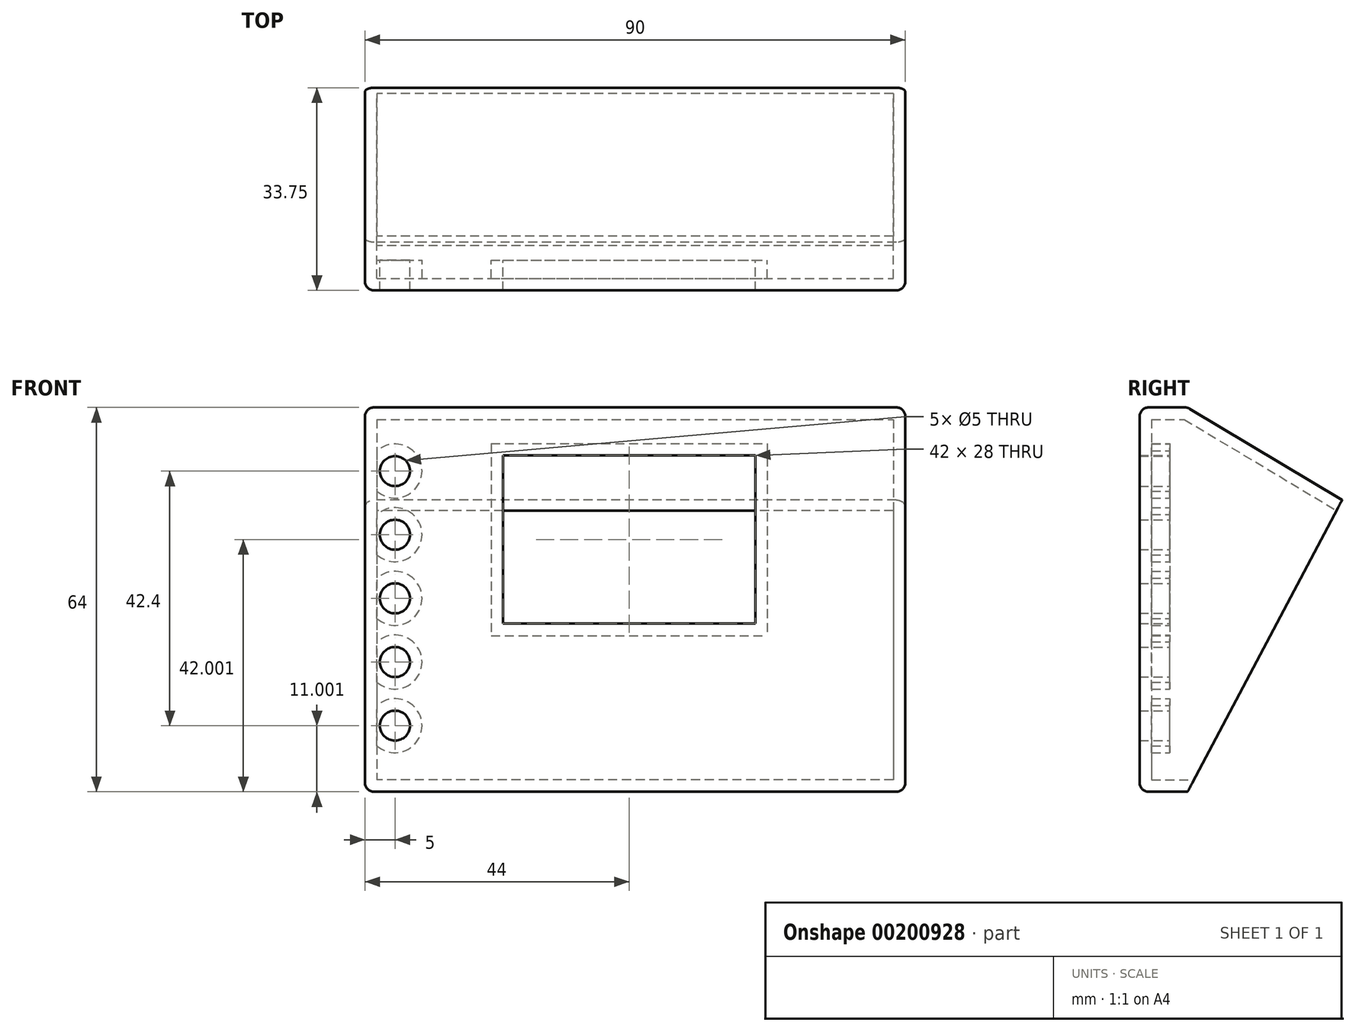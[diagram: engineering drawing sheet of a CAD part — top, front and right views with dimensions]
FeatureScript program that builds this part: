
annotation { "Feature Type Name" : "Feature", "Feature Type Description" : "" }
export const myFeature = defineFeature(function(context is Context, id is Id, definition is map)
    precondition{}
    {
        {
            var Q0;
            Q0=qCreatedBy(makeId("Front.planeOp"),FACE);
            var sketch = newSketch(context, id + "F0", { "sketchPlane" : qUnion([Q0])});
            skLineSegment(sketch, "E0.bottom", {"start": v(-41, 33.96) * mm, "end": v(49, 33.96) * mm});
            skLineSegment(sketch, "E0.top", {"start": v(-41, -30.04) * mm, "end": v(49, -30.04) * mm});
            skLineSegment(sketch, "E0.left", {"start": v(-41, 33.96) * mm, "end": v(-41, -30.04) * mm});
            skLineSegment(sketch, "E0.right", {"start": v(49, 33.96) * mm, "end": v(49, -30.04) * mm});
            skCircle(sketch, "E1", {"center": v(-36, 23.36) * mm, "radius": 2.5 * mm});
            skCircle(sketch, "E2", {"center": v(-36, 12.76) * mm, "radius": 2.5 * mm});
            skCircle(sketch, "E3", {"center": v(-36, 2.16) * mm, "radius": 2.5 * mm});
            skCircle(sketch, "E4", {"center": v(-36, -8.44) * mm, "radius": 2.5 * mm});
            skCircle(sketch, "E5", {"center": v(-36, -19.04) * mm, "radius": 2.5 * mm});
            skLineSegment(sketch, "E6.bottom", {"start": v(-18, 25.96) * mm, "end": v(24, 25.96) * mm});
            skLineSegment(sketch, "E6.top", {"start": v(-18, -2.04) * mm, "end": v(24, -2.04) * mm});
            skLineSegment(sketch, "E6.left", {"start": v(-18, 25.96) * mm, "end": v(-18, -2.04) * mm});
            skLineSegment(sketch, "E6.right", {"start": v(24, 25.96) * mm, "end": v(24, -2.04) * mm});
            skSolve(sketch);
        }
        {
            var Q0;
            Q0=makeQuery(id+"F0.imprint","IMPRINT",FACE,{"disambiguationData":[TD([[makeQuery(id+"F0.imprint","IMPRINT",EDGE,{"derivedFrom":sQuery(id+"F0.wireOp",EDGE,"E0.bottom")}),-1.0]])]});
            extrude(context, id + "F1", {"entities" : qUnion([Q0]), "depth" : 3 * mm});
        }
        {
            var Q0;
            Q0=makeQuery(id+"F1.opExtrude","SWEPT_FACE",FACE,{"disambiguationData":[OSD([sQuery(id+"F0.wireOp",EDGE,"E0.left")])]});
            cPlane(context, id + "F2", {"entities" : qUnion([Q0]), "cplaneType" : CPlaneType.OFFSET, "offset" : 0 * mm, "width" : 150 * mm, "height" : 150 * mm});
        }
        {
            var Q0;
            Q0=qCreatedBy(id+"F2.planeOp",FACE);
            var sketch = newSketch(context, id + "F3", { "sketchPlane" : qUnion([Q0])});
            skLineSegment(sketch, "E7", {"start": v(0, 33.96) * mm, "end": v(-5, 33.96) * mm});
            skLineSegment(sketch, "E8", {"start": v(-5, 33.96) * mm, "end": v(-30.75, 18.56) * mm});
            skLineSegment(sketch, "E9", {"start": v(-30.75, 18.56) * mm, "end": v(-5, -30.04) * mm});
            skLineSegment(sketch, "E10", {"start": v(-5, -30.04) * mm, "end": v(0, -30.04) * mm});
            skLineSegment(sketch, "E11", {"start": v(0, -30.04) * mm, "end": v(0, 33.96) * mm});
            skSolve(sketch);
        }
        {
            var Q0;
            Q0=makeQuery(id+"F3.imprint","IMPRINT",FACE,{"disambiguationData":[TD([[makeQuery(id+"F3.imprint","IMPRINT",EDGE,{"derivedFrom":sQuery(id+"F3.wireOp",EDGE,"E7")}),1.0]])]});
            extrude(context, id + "F4", {"entities" : qUnion([Q0]), "operationType" : NewBodyOperationType.ADD, "oppositeDirection" : true, "depth" : 90 * mm});
        }
        {
            var Q0;
            Q0=makeQuery(id+"F4.opExtrude","SWEPT_FACE",FACE,{"disambiguationData":[OSD([sQuery(id+"F3.wireOp",EDGE,"E9")])]});
            shell(context, id + "F5", {"entities" : qUnion([Q0]), "thickness" : 2 * mm});
        }
        {
            var Q0;
            Q0=makeQuery(id+"F0.imprint","IMPRINT",FACE,{"disambiguationData":[TD([[makeQuery(id+"F0.imprint","IMPRINT",EDGE,{"derivedFrom":sQuery(id+"F0.wireOp",EDGE,"E1")}),1.0]])]});
            var Q1;
            Q1=makeQuery(id+"F0.imprint","IMPRINT",FACE,{"disambiguationData":[TD([[makeQuery(id+"F0.imprint","IMPRINT",EDGE,{"derivedFrom":sQuery(id+"F0.wireOp",EDGE,"E2")}),1.0]])]});
            var Q2;
            Q2=makeQuery(id+"F0.imprint","IMPRINT",FACE,{"disambiguationData":[TD([[makeQuery(id+"F0.imprint","IMPRINT",EDGE,{"derivedFrom":sQuery(id+"F0.wireOp",EDGE,"E3")}),1.0]])]});
            var Q3;
            Q3=makeQuery(id+"F0.imprint","IMPRINT",FACE,{"disambiguationData":[TD([[makeQuery(id+"F0.imprint","IMPRINT",EDGE,{"derivedFrom":sQuery(id+"F0.wireOp",EDGE,"E4")}),1.0]])]});
            var Q4;
            Q4=makeQuery(id+"F0.imprint","IMPRINT",FACE,{"disambiguationData":[TD([[makeQuery(id+"F0.imprint","IMPRINT",EDGE,{"derivedFrom":sQuery(id+"F0.wireOp",EDGE,"E5")}),1.0]])]});
            var Q5;
            Q5=makeQuery(id+"F0.imprint","IMPRINT",FACE,{"disambiguationData":[TD([[makeQuery(id+"F0.imprint","IMPRINT",EDGE,{"derivedFrom":sQuery(id+"F0.wireOp",EDGE,"E6.bottom")}),-1.0]])]});
            extrude(context, id + "F6", {"entities" : qUnion([Q0, Q1, Q2, Q3, Q4, Q5]), "operationType" : NewBodyOperationType.REMOVE, "oppositeDirection" : true, "depth" : 5 * mm});
        }
        {
            var Q0;
            Q0=makeQuery(id+"F1.opExtrude","CAP_EDGE",EDGE,{"disambiguationData":[OSD([sQuery(id+"F0.wireOp",EDGE,"E0.right")])],"isStart":false});
            var Q1;
            Q1=makeQuery(id+"F4.boolean.opBoolean","MERGE",EDGE,{"derivedFrom":[makeQuery(id+"F1.opExtrude","SWEPT_EDGE",EDGE,{"disambiguationData":[OSD([sQuery(id+"F0.wireOp",EDGE,"E0.top"),sQuery(id+"F0.wireOp",EDGE,"E0.right")])]}),makeQuery(id+"F4.opExtrude","CAP_EDGE",EDGE,{"disambiguationData":[OSD([sQuery(id+"F3.wireOp",EDGE,"E10")])],"isStart":false})]});
            var Q2;
            Q2=makeQuery(id+"F1.opExtrude","CAP_EDGE",EDGE,{"disambiguationData":[OSD([sQuery(id+"F0.wireOp",EDGE,"E0.top")])],"isStart":false});
            var Q3;
            Q3=makeQuery(id+"F4.boolean.opBoolean","MERGE",EDGE,{"derivedFrom":[makeQuery(id+"F1.opExtrude","SWEPT_EDGE",EDGE,{"disambiguationData":[OSD([sQuery(id+"F0.wireOp",EDGE,"E0.bottom"),sQuery(id+"F0.wireOp",EDGE,"E0.right")])]}),makeQuery(id+"F4.opExtrude","CAP_EDGE",EDGE,{"disambiguationData":[OSD([sQuery(id+"F3.wireOp",EDGE,"E7")])],"isStart":false})]});
            var Q4;
            Q4=makeQuery(id+"F4.opExtrude","CAP_EDGE",EDGE,{"disambiguationData":[OSD([sQuery(id+"F3.wireOp",EDGE,"E8")])],"isStart":false});
            var Q5;
            Q5=makeQuery(id+"F1.opExtrude","CAP_EDGE",EDGE,{"disambiguationData":[OSD([sQuery(id+"F0.wireOp",EDGE,"E0.bottom")])],"isStart":false});
            var Q6;
            Q6=makeQuery(id+"F4.opExtrude","SWEPT_EDGE",EDGE,{"disambiguationData":[OSD([sQuery(id+"F3.wireOp",EDGE,"E7"),sQuery(id+"F3.wireOp",EDGE,"E8")])]});
            var Q7;
            Q7=makeQuery(id+"F1.opExtrude","CAP_EDGE",EDGE,{"disambiguationData":[OSD([sQuery(id+"F0.wireOp",EDGE,"E0.left")])],"isStart":false});
            var Q8;
            Q8=makeQuery(id+"F4.boolean.opBoolean","MERGE",EDGE,{"derivedFrom":[makeQuery(id+"F1.opExtrude","SWEPT_EDGE",EDGE,{"disambiguationData":[OSD([sQuery(id+"F0.wireOp",EDGE,"E0.bottom"),sQuery(id+"F0.wireOp",EDGE,"E0.left")])]}),makeQuery(id+"F4.opExtrude","CAP_EDGE",EDGE,{"disambiguationData":[OSD([sQuery(id+"F3.wireOp",EDGE,"E7")])],"isStart":true})]});
            var Q9;
            Q9=makeQuery(id+"F4.opExtrude","CAP_EDGE",EDGE,{"disambiguationData":[OSD([sQuery(id+"F3.wireOp",EDGE,"E8")])],"isStart":true});
            var Q10;
            Q10=makeQuery(id+"F4.boolean.opBoolean","MERGE",EDGE,{"derivedFrom":[makeQuery(id+"F1.opExtrude","SWEPT_EDGE",EDGE,{"disambiguationData":[OSD([sQuery(id+"F0.wireOp",EDGE,"E0.top"),sQuery(id+"F0.wireOp",EDGE,"E0.left")])]}),makeQuery(id+"F4.opExtrude","CAP_EDGE",EDGE,{"disambiguationData":[OSD([sQuery(id+"F3.wireOp",EDGE,"E10")])],"isStart":true})]});
            fillet(context, id + "F7", {"entities" : qUnion([Q0, Q1, Q2, Q3, Q4, Q5, Q6, Q7, Q8, Q9, Q10]), "radius" : 1.5 * mm, "tangentPropagation" : true, "allowEdgeOverflow" : false});
        }
        {
            var Q0;
            Q0=makeQuery(id+"F1.opExtrude","SWEPT_BODY",BODY,{"disambiguationData":[OSD([sQuery(id+"F0.wireOp",EDGE,"E0.bottom"),sQuery(id+"F0.wireOp",EDGE,"E0.top"),sQuery(id+"F0.wireOp",EDGE,"E0.left"),sQuery(id+"F0.wireOp",EDGE,"E0.right"),sQuery(id+"F0.wireOp",EDGE,"E1"),sQuery(id+"F0.wireOp",EDGE,"E2"),sQuery(id+"F0.wireOp",EDGE,"E3"),sQuery(id+"F0.wireOp",EDGE,"E4"),sQuery(id+"F0.wireOp",EDGE,"E5"),sQuery(id+"F0.wireOp",EDGE,"E6.bottom"),sQuery(id+"F0.wireOp",EDGE,"E6.top"),sQuery(id+"F0.wireOp",EDGE,"E6.left"),sQuery(id+"F0.wireOp",EDGE,"E6.right")])]});
            transform(context, id + "F8", {"entities" : qUnion([Q0]), "transformType" : TransformType.TRANSLATION_3D, "dx" : 0 * mm, "dy" : 0 * mm, "dz" : 0 * mm, "makeCopy" : true});
        }
        {
            var Q0;
            Q0=makeQuery(id+"F8.opPattern","COPY",BODY,{"derivedFrom":makeQuery(id+"F1.opExtrude","SWEPT_BODY",BODY,{"disambiguationData":[OSD([sQuery(id+"F0.wireOp",EDGE,"E0.bottom"),sQuery(id+"F0.wireOp",EDGE,"E0.top"),sQuery(id+"F0.wireOp",EDGE,"E0.left"),sQuery(id+"F0.wireOp",EDGE,"E0.right"),sQuery(id+"F0.wireOp",EDGE,"E1"),sQuery(id+"F0.wireOp",EDGE,"E2"),sQuery(id+"F0.wireOp",EDGE,"E3"),sQuery(id+"F0.wireOp",EDGE,"E4"),sQuery(id+"F0.wireOp",EDGE,"E5"),sQuery(id+"F0.wireOp",EDGE,"E6.bottom"),sQuery(id+"F0.wireOp",EDGE,"E6.top"),sQuery(id+"F0.wireOp",EDGE,"E6.left"),sQuery(id+"F0.wireOp",EDGE,"E6.right")])]}),"instanceName":"1"});
            deleteBodies(context, id + "F9", {"entities" : qUnion([Q0])});
        }
    });
